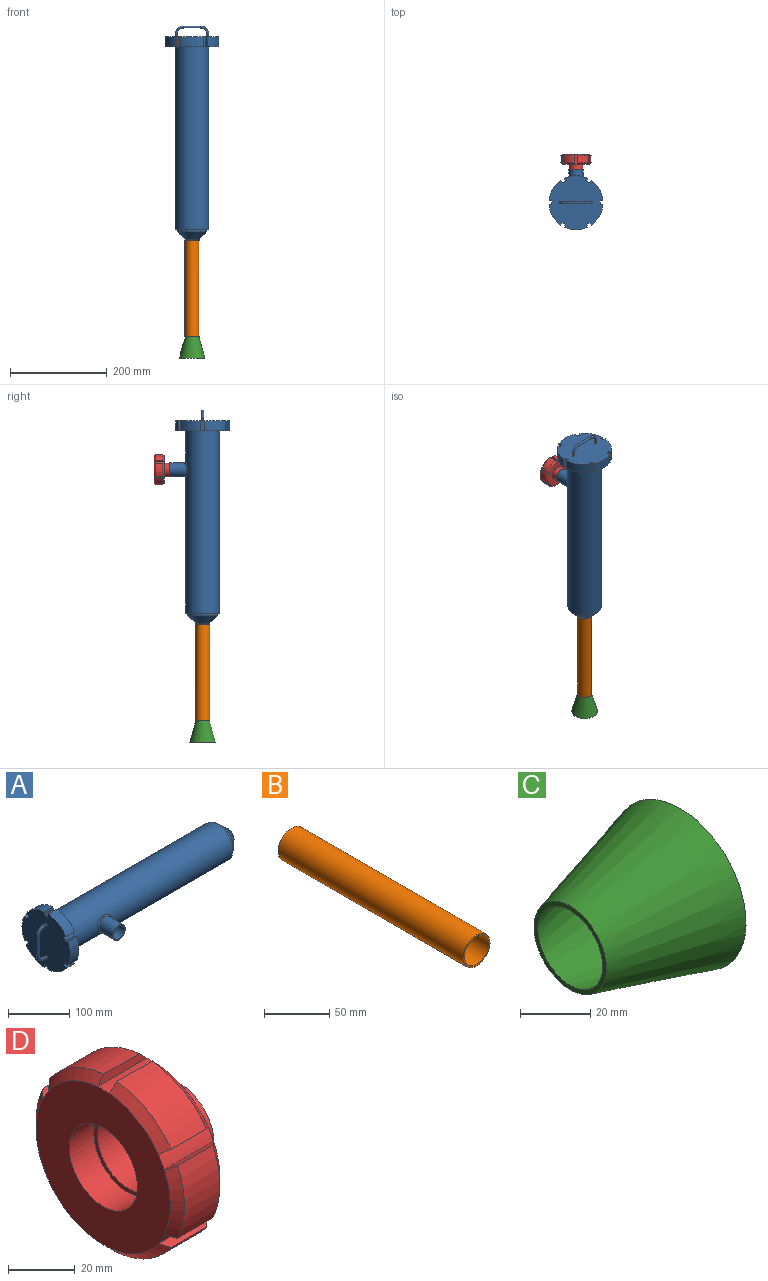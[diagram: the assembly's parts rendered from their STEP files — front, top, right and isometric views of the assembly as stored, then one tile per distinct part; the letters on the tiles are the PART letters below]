
ASSEMBLY  parts=4 mates=3
PART A: 47 faces, bbox 444.9x124x111.7 mm
  f0: cylinder r=13mm len=401mm, axis (1,0,0), area 31867.6mm2, adj f10,f11,f41,f42,f44,f45
  f1: cylinder r=35mm len=378mm, axis (1,0,0), area 82220.3mm2, adj f3,f15,f46
  f2: plane 112x111.67mm, normal (-1,0,0), area 9518.9mm2, adj f4,f5,f6,f7,f8,f9,f16,f20
  f3: plane 112x111.67mm, normal (1,0,0), area 5709.8mm2, adj f1,f4,f5,f6,f7,f8,f9,f21
  f4: cylinder r=56mm len=41.89mm, axis (1,0,0), area 1000.4mm2, adj f2,f3,f34,f36
  f5: cylinder r=56mm len=48.37mm, axis (1,0,0), area 1000.4mm2, adj f2,f3,f31,f35
  f6: cylinder r=56mm len=41.89mm, axis (1,0,0), area 1000.4mm2, adj f2,f3,f28,f32
  f7: cylinder r=56mm len=41.89mm, axis (1,0,0), area 1000.4mm2, adj f2,f3,f25,f29
  f8: cylinder r=56mm len=48.37mm, axis (1,0,0), area 1000.4mm2, adj f2,f3,f22,f26
  f9: cylinder r=56mm len=41.89mm, axis (1,0,0), area 1000.4mm2, adj f2,f3,f23,f38
  f10: plane 26x26mm, normal (1,0,0), area 530.9mm2, adj f0
  f11: plane 29x29mm, normal (1,0,0), area 129.6mm2, adj f0,f12
  f12: cylinder r=14.5mm len=29mm, axis (1,0,0), area 205.5mm2, adj f11,f13
  f13: cone r=30.79mm half-angle=47.9deg, axis (-1,0,0), area 3124.2mm2, adj f12,f14
  f14: cylinder r=30.79mm len=61.59mm, axis (1,0,0), area 1166.6mm2, adj f13,f15
  f15: plane 70x70mm, normal (1,0,0), area 869.3mm2, adj f1,f14
  f16: cylinder r=2.5mm len=5mm, axis (-1,0,0), area 78.5mm2, adj f2,f17
  f17: torus R=15mm, axis (0,-1,0), area 370.1mm2, adj f16,f18
  f18: cylinder r=2.5mm len=35mm, axis (0,0,-1), area 549.8mm2, adj f17,f19
  f19: torus R=15mm, axis (0,-1,0), area 370.1mm2, adj f18,f20
  f20: cylinder r=2.5mm len=5mm, axis (1,0,0), area 78.5mm2, adj f2,f19
  f21: cylinder r=50mm len=20mm, axis (-1,0,0), area 154mm2, adj f2,f3,f22,f23
  f22: plane 20x5.41mm, normal (0,0.43,0.9), area 120mm2, adj f2,f3,f8,f21
  f23: plane 20x4.95mm, normal (0,-0.57,-0.82), area 120mm2, adj f2,f3,f9,f21
  f24: cylinder r=50mm len=20mm, axis (-1,0,0), area 154mm2, adj f2,f3,f25,f26
  f25: plane 20x4.95mm, normal (0,-0.57,0.82), area 120mm2, adj f2,f3,f7,f24
  f26: plane 20x5.41mm, normal (0,0.43,-0.9), area 120mm2, adj f2,f3,f8,f24
  f27: cylinder r=50mm len=20mm, axis (-1,0,0), area 154mm2, adj f2,f3,f28,f29
  f28: plane 20x5.98mm, normal (0,-1,-0.08), area 120mm2, adj f2,f3,f6,f27
  f29: plane 20x5.98mm, normal (0,1,-0.08), area 120mm2, adj f2,f3,f7,f27
  f30: cylinder r=50mm len=20mm, axis (-1,0,0), area 154mm2, adj f2,f3,f31,f32
  f31: plane 20x5.41mm, normal (0,-0.43,-0.9), area 120mm2, adj f2,f3,f5,f30
  f32: plane 20x4.95mm, normal (0,0.57,0.82), area 120mm2, adj f2,f3,f6,f30
  f33: cylinder r=50mm len=20mm, axis (-1,0,0), area 154mm2, adj f2,f3,f34,f35
  f34: plane 20x4.95mm, normal (0,0.57,-0.82), area 120mm2, adj f2,f3,f4,f33
  f35: plane 20x5.41mm, normal (0,-0.43,0.9), area 120mm2, adj f2,f3,f5,f33
  f36: plane 20x5.98mm, normal (0,-1,0.08), area 120mm2, adj f2,f3,f4,f37
  f37: cylinder r=50mm len=20mm, axis (-1,0,0), area 154mm2, adj f2,f3,f36,f38
  f38: plane 20x5.98mm, normal (0,1,0.08), area 120mm2, adj f2,f3,f9,f37
  f39: plane 29x29mm, normal (0,-1,0), area 129.6mm2, adj f40,f43
  f40: cylinder r=14.5mm len=34.27mm, axis (0,1,0), area 2924.8mm2, adj f39,f46
  f41: plane 26x14.5mm, normal (0,1,0), area 51.8mm2, adj f0,f42,f43
  f42: cylinder r=14.5mm len=26mm, axis (0,1,0), area 307.5mm2, adj f0,f41
  f43: cylinder r=13mm len=68mm, axis (0,1,0), area 5554.3mm2, adj f39,f41,f44
  f44: plane 26x14.5mm, normal (0,1,0), area 51.8mm2, adj f0,f43,f45
  f45: cylinder r=14.5mm len=26mm, axis (0,1,0), area 307.5mm2, adj f0,f44
  f46: bspline ~35.01x32.25mm, area 390.1mm2, adj f1,f40
PART B: 4 faces, bbox 29x200x29 mm
  f0: plane 29x29mm, normal (0,-1,0), area 129.6mm2, adj f2,f3
  f1: plane 29x29mm, normal (0,1,0), area 129.6mm2, adj f2,f3
  f2: cylinder r=13mm len=200mm, axis (0,1,0), area 16336.3mm2, adj f0,f1
  f3: cylinder r=14.5mm len=200mm, axis (0,1,0), area 18221.2mm2, adj f0,f1
PART C: 4 faces, bbox 44x53.1x53.1 mm
  f0: plane 29.11x29.11mm, normal (-1,0,0), area 134.6mm2, adj f1,f3
  f1: cone r=25mm half-angle=15.3deg, axis (1,0,0), area 5444.6mm2, adj f0,f2
  f2: plane 53.11x53.11mm, normal (1,0,0), area 251.8mm2, adj f1,f3
  f3: cone r=14.55mm half-angle=15.3deg, axis (1,0,0), area 5890.1mm2, adj f0,f2
PART D: 43 faces, bbox 32.5x63x62.8 mm
  f0: cylinder r=31.5mm len=23.06mm, axis (-1,0,0), area 412.3mm2, adj f7,f13,f37,f41
  f1: cylinder r=31.5mm len=26.63mm, axis (-1,0,0), area 412.3mm2, adj f8,f14,f34,f39
  f2: cylinder r=31.5mm len=23.06mm, axis (-1,0,0), area 412.3mm2, adj f9,f15,f31,f36
  f3: cylinder r=31.5mm len=23.06mm, axis (-1,0,0), area 412.3mm2, adj f10,f16,f28,f33
  f4: cylinder r=31.5mm len=26.63mm, axis (-1,0,0), area 412.3mm2, adj f11,f17,f25,f30
  f5: cylinder r=31.5mm len=23.06mm, axis (-1,0,0), area 412.3mm2, adj f6,f12,f27,f42
  f6: cone r=31.5mm half-angle=45deg, axis (-1,0,0), area 111.1mm2, adj f5,f24,f27,f42
  f7: cone r=31.5mm half-angle=45deg, axis (-1,0,0), area 111.1mm2, adj f0,f24,f37,f41
  f8: cone r=31.5mm half-angle=45deg, axis (-1,0,0), area 111.1mm2, adj f1,f24,f34,f39
  f9: cone r=31.5mm half-angle=45deg, axis (-1,0,0), area 111.1mm2, adj f2,f24,f31,f36
  f10: cone r=31.5mm half-angle=45deg, axis (-1,0,0), area 111.1mm2, adj f3,f24,f28,f33
  f11: cone r=31.5mm half-angle=45deg, axis (-1,0,0), area 111.1mm2, adj f4,f24,f25,f30
  f12: cone r=28.5mm half-angle=45deg, axis (1,0,0), area 111.1mm2, adj f5,f18,f27,f42
  f13: cone r=28.5mm half-angle=45deg, axis (1,0,0), area 111.1mm2, adj f0,f18,f37,f41
  f14: cone r=28.5mm half-angle=45deg, axis (1,0,0), area 111.1mm2, adj f1,f18,f34,f39
  f15: cone r=28.5mm half-angle=45deg, axis (1,0,0), area 111.1mm2, adj f2,f18,f31,f36
  f16: cone r=28.5mm half-angle=45deg, axis (1,0,0), area 111.1mm2, adj f3,f18,f28,f33
  f17: cone r=28.5mm half-angle=45deg, axis (1,0,0), area 111.1mm2, adj f4,f18,f25,f30
  f18: plane 57x57mm, normal (-1,0,0), area 1891.2mm2, adj f12,f13,f14,f15,f16,f17,f19,f26
  f19: cylinder r=14.5mm len=29mm, axis (-1,0,0), area 956.6mm2, adj f18,f20
  f20: plane 29x29mm, normal (-1,0,0), area 129.6mm2, adj f19,f21
  f21: cylinder r=13mm len=26mm, axis (-1,0,0), area 1797mm2, adj f20,f22
  f22: plane 29x29mm, normal (1,0,0), area 129.6mm2, adj f21,f23
  f23: cylinder r=14.5mm len=29mm, axis (-1,0,0), area 1047.7mm2, adj f22,f24
  f24: plane 57x57mm, normal (1,0,0), area 1891.2mm2, adj f6,f7,f8,f9,f10,f11,f23,f26
  f25: plane 21x2.72mm, normal (0,-0.42,0.91), area 54mm2, adj f4,f11,f17,f26
  f26: cylinder r=28.5mm len=21mm, axis (-1,0,0), area 104.5mm2, adj f18,f24,f25,f27
  f27: plane 21x2.46mm, normal (0,0.57,-0.82), area 54mm2, adj f5,f6,f12,f26
  f28: plane 21x2.46mm, normal (0,0.57,0.82), area 54mm2, adj f3,f10,f16,f29
  f29: cylinder r=28.5mm len=21mm, axis (-1,0,0), area 104.5mm2, adj f18,f24,f28,f30
  f30: plane 21x2.72mm, normal (0,-0.42,-0.91), area 54mm2, adj f4,f11,f17,f29
  f31: plane 21x2.99mm, normal (0,1,-0.09), area 54mm2, adj f2,f9,f15,f32
  f32: cylinder r=28.5mm len=21mm, axis (-1,0,0), area 104.5mm2, adj f18,f24,f31,f33
  f33: plane 21x2.99mm, normal (0,-1,-0.09), area 54mm2, adj f3,f10,f16,f32
  f34: plane 21x2.72mm, normal (0,0.42,-0.91), area 54mm2, adj f1,f8,f14,f35
  f35: cylinder r=28.5mm len=21mm, axis (-1,0,0), area 104.5mm2, adj f18,f24,f34,f36
  f36: plane 21x2.46mm, normal (0,-0.57,0.82), area 54mm2, adj f2,f9,f15,f35
  f37: plane 21x2.46mm, normal (0,-0.57,-0.82), area 54mm2, adj f0,f7,f13,f38
  f38: cylinder r=28.5mm len=21mm, axis (-1,0,0), area 104.5mm2, adj f18,f24,f37,f39
  f39: plane 21x2.72mm, normal (0,0.42,0.91), area 54mm2, adj f1,f8,f14,f38
  f40: cylinder r=28.5mm len=21mm, axis (-1,0,0), area 104.5mm2, adj f18,f24,f41,f42
  f41: plane 21x2.99mm, normal (0,1,0.09), area 54mm2, adj f0,f7,f13,f40
  f42: plane 21x2.99mm, normal (0,-1,0.09), area 54mm2, adj f5,f6,f12,f40
PLACE A rot(axis=(-0.71,0,0.71),180deg) t=(823.43,-501.25,761.91)mm
PLACE B rot(axis=(0.58,-0.58,-0.58),120deg) t=(823.43,-146.71,761.91)mm
PLACE C rot(axis=(0,1,0),90deg) t=(823.43,-501.25,561.91)mm
PLACE D rot(axis=(0.71,-0.71,0),180deg) t=(823.43,-400.75,1081.91)mm
MATE cylindrical D.f0 <-> A.f40  axis (0,-1,0) through (823.43,-433.25,1081.91)mm
MATE cylindrical A.f0 <-> C.f1  axis (0,0,-1) through (823.43,-501.25,761.91)mm
MATE cylindrical B.f2 <-> A.f0  axis (0,0,1) through (823.43,-501.25,761.91)mm
